# Revit family: BLAUBERG-KOMFORT_EC_S160_SB160
name_source: partatom
category: Mechanical Equipment
units: mm (PartAtom-declared; Revit-internal decimal feet)

## family parameters
Always vertical = Yes
Classification = None
Cut with Voids When Loaded = No
OmniClass Number = 23.75.35.14
OmniClass Title = Air Handling Units
Part Type = Normal
Room Calculation Point = No
Round Connector Dimension = Use Diameter
Shared = No
Work Plane-Based = No

## types (8) — shared parameters
B = 340 mm  [stored 1.11549 ft]
B1 = 330 mm
B3 = 14 mm  [stored 0.0459318 ft]
BackFeetD = 20 mm  [stored 0.0656168 ft]
Casing Material = Painted Steel White
Current = 1 A
D = 125 mm  [stored 0.410105 ft]
Description = Air Handling Unit
DrainConB = 164 mm  [stored 0.538058 ft]
Duct Connection Diameter = 125 mm  [stored 0.410105 ft]
ElBoxA = 146 mm  [stored 0.479003 ft]
ElBoxB = 270 mm  [stored 0.885827 ft]
ElConA = 280 mm  [stored 0.918635 ft]
Extract Air Filter = G4
Family Version = 1.0
Front Maintenance Zone Height = 600 mm  [stored 1.9685 ft]
Front Maintenance Zone Length = 600 mm  [stored 1.9685 ft]
H3 = 60 mm  [stored 0.19685 ft]
HDuctCon = 50 mm  [stored 0.164042 ft]
Heat Exchanger Type = counter-flow
L = 600 mm  [stored 1.9685 ft]
L1 = 388 mm  [stored 1.27297 ft]
L2 = 143 mm
Load Classification = HVAC
Maintenance Zone Material = Maintenance Zone
Manufacturer = Blauberg
Maximum Air Flow = 200 m³/h
Metal Material = Metal Zinc
Number of Poles = 1
Plastic Material = Polypropylene Black
Power = 57 W
Power Factor = 1
RPM (min-1) = 3770
Sound Pressure Level at 3 m (dBA) = 24
Supply Air Filter = F7 (optionally G4)
Transported Air Temperature (°C) = –25 …+40
URL = https://blaubergventilatoren.de
Voltage = 230 V
dBFeets = 64 mm  [stored 0.209974 ft]
dLFeets = 45 mm  [stored 0.147638 ft]

## per-type parameters (varying)
| type | Ddrain | Drain Connection Diameter | DrainPipe | Front Maintenance Zone Width | H1 | Heat Exchanger Material | Heat recovery efficiency (%) | Model | SEC Class | Type Comments | Weight |
| KOMFORT EC S160 S21 | 18 mm  [stored 0.0590551 ft] | 18 mm  [stored 0.0590551 ft] | Yes | 550 mm | 550 mm | polystyrene | 85..93 | KOMFORT EC S160 S21 | A+ | Air Handling Unit KOMFORT EC S160 S21 | 34.00 kg |
| KOMFORT EC S160 S14 | 18 mm  [stored 0.0590551 ft] | 18 mm  [stored 0.0590551 ft] | Yes | 550 mm | 550 mm | polystyrene | 85..93 | KOMFORT EC S160 S14 | A+ | Air Handling Unit KOMFORT EC S160 S14 | 34.00 kg |
| KOMFORT EC S160-E S21 | 1 mm  [stored 0.00328084 ft] | 0 mm  [stored 0 ft] | No | 550 mm | 550 mm | enthalpy | 76..92 | KOMFORT EC S160-E S21 | A | Air Handling Unit KOMFORT EC S160-E S21 | 34.00 kg |
| KOMFORT EC S160-E S14 | 1 mm  [stored 0.00328084 ft] | 0 mm  [stored 0 ft] | No | 550 mm | 550 mm | enthalpy | 76..92 | KOMFORT EC S160-E S14 | A | Air Handling Unit KOMFORT EC S160-E S14 | 34.00 kg |
| KOMFORT EC SB160 S21 | 18 mm  [stored 0.0590551 ft] | 18 mm  [stored 0.0590551 ft] | Yes | 580 mm  [stored 1.90289 ft] | 580 mm  [stored 1.90289 ft] | polystyrene | 85..93 | KOMFORT EC S160-E S14 | A+ | Air Handling Unit KOMFORT EC S160-E S14 | 36.00 kg |
| KOMFORT EC SB160 S14 | 18 mm  [stored 0.0590551 ft] | 18 mm  [stored 0.0590551 ft] | Yes | 580 mm  [stored 1.90289 ft] | 580 mm  [stored 1.90289 ft] | polystyrene | 85..93 | KOMFORT EC SB160 S21 | A+ | Air Handling Unit KOMFORT EC SB160 S21 | 36.00 kg |
| KOMFORT EC SB160-E S21 | 1 mm  [stored 0.00328084 ft] | 0 mm  [stored 0 ft] | No | 580 mm  [stored 1.90289 ft] | 580 mm  [stored 1.90289 ft] | enthalpy | 76..92 | KOMFORT EC SB160-E S21 | A | Air Handling Unit KOMFORT EC SB160-E S21 | 36.00 kg |
| KOMFORT EC SB160-E S14 | 1 mm  [stored 0.00328084 ft] | 0 mm  [stored 0 ft] | No | 580 mm  [stored 1.90289 ft] | 580 mm  [stored 1.90289 ft] | enthalpy | 76..92 | KOMFORT EC SB160 S14 | A | Air Handling Unit KOMFORT EC SB160 S14 | 36.00 kg |

note: [stored X ft] marks values corroborated as IEEE doubles in the binary element streams (Revit-internal decimal feet)

## geometry (parser evidence)
native form markers: Sweep x5
no freeform markers — native parametric forms only
